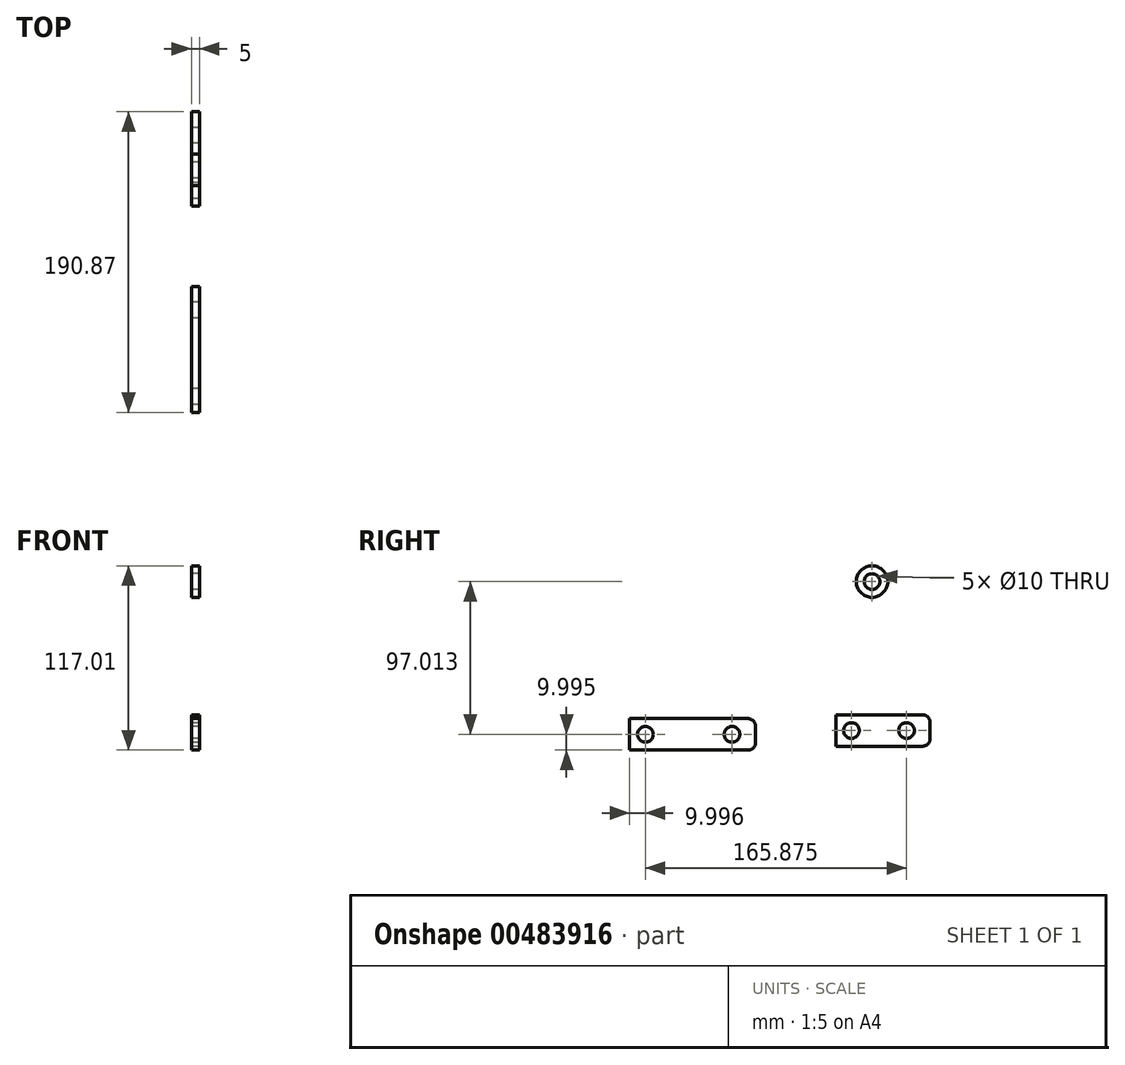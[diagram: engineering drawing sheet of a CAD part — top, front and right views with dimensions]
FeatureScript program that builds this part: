
annotation { "Feature Type Name" : "Feature", "Feature Type Description" : "" }
export const myFeature = defineFeature(function(context is Context, id is Id, definition is map)
    precondition{}
    {
        {
            var Q0;
            Q0=qCreatedBy(makeId("Right.planeOp"),FACE);
            var sketch = newSketch(context, id + "F0", { "sketchPlane" : qUnion([Q0])});
            skLineSegment(sketch, "E0", {"start": v(-147.7, -259.2) * mm, "end": v(-92.7, -259.2) * mm});
            skLineSegment(sketch, "E1", {"start": v(-87.7, -264.2) * mm, "end": v(-87.7, -274.2) * mm});
            skLineSegment(sketch, "E2", {"start": v(-92.7, -279.2) * mm, "end": v(-147.7, -279.2) * mm});
            skPoint(sketch, "E3.visualSharp", {"position": v(-87.7, -259.2) * mm});
            skArc(sketch, "E3.filletArc", {"start": v(-87.7, -264.2) * mm, "mid": v(-89.17, -260.66) * mm, "end": v(-92.7, -259.2) * mm});
            skPoint(sketch, "E4.visualSharp", {"position": v(-87.7, -279.2) * mm});
            skArc(sketch, "E4.filletArc", {"start": v(-92.7, -279.2) * mm, "mid": v(-89.17, -277.73) * mm, "end": v(-87.7, -274.2) * mm});
            skLineSegment(sketch, "E5", {"start": v(-147.7, -259.2) * mm, "end": v(-147.7, -279.2) * mm});
            skCircle(sketch, "E6", {"center": v(-102.7, -269.2) * mm, "radius": 5 * mm});
            skLineSegment(sketch, "E7", {"start": v(-278.58, -261.58) * mm, "end": v(-203.58, -261.58) * mm});
            skLineSegment(sketch, "E8", {"start": v(-198.58, -266.58) * mm, "end": v(-198.58, -276.58) * mm});
            skLineSegment(sketch, "E9", {"start": v(-203.58, -281.58) * mm, "end": v(-278.58, -281.58) * mm});
            skPoint(sketch, "E10.visualSharp", {"position": v(-198.58, -261.58) * mm});
            skArc(sketch, "E10.filletArc", {"start": v(-198.58, -266.58) * mm, "mid": v(-200.05, -263.05) * mm, "end": v(-203.58, -261.58) * mm});
            skPoint(sketch, "E11.visualSharp", {"position": v(-198.58, -281.58) * mm});
            skArc(sketch, "E11.filletArc", {"start": v(-203.58, -281.58) * mm, "mid": v(-200.05, -280.12) * mm, "end": v(-198.58, -276.58) * mm});
            skLineSegment(sketch, "E12", {"start": v(-278.58, -261.58) * mm, "end": v(-278.58, -281.58) * mm});
            skCircle(sketch, "E13", {"center": v(-213.58, -271.58) * mm, "radius": 5 * mm});
            skLineSegment(sketch, "E14", {"start": v(-278.58, -271.58) * mm, "end": v(-268.58, -271.58) * mm, "construction": true});
            skLineSegment(sketch, "E15", {"start": v(-147.7, -269.2) * mm, "end": v(-137.7, -269.2) * mm, "construction": true});
            skCircle(sketch, "E16", {"center": v(-137.7, -269.2) * mm, "radius": 5 * mm});
            skCircle(sketch, "E17", {"center": v(-268.58, -271.58) * mm, "radius": 5 * mm});
            skCircle(sketch, "E18", {"center": v(-124.63, -174.57) * mm, "radius": 10 * mm});
            skCircle(sketch, "E19", {"center": v(-124.63, -174.57) * mm, "radius": 5 * mm});
            skSolve(sketch);
        }
        {
            var Q0;
            Q0 = qSketchRegion(id + "F0", true);
            extrude(context, id + "F1", {"entities" : qUnion([Q0]), "depth" : 5 * mm});
        }
    });
